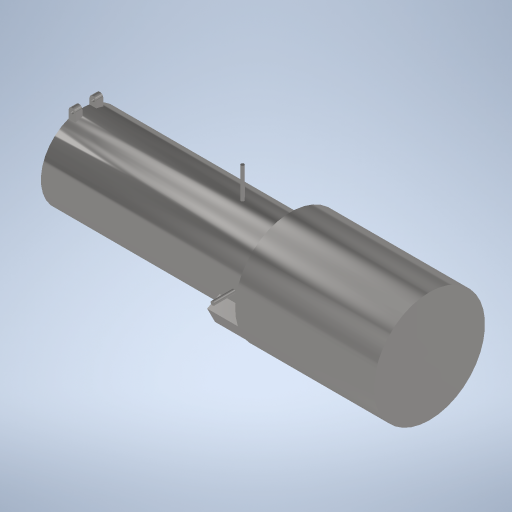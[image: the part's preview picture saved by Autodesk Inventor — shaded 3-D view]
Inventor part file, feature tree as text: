
AUTODESK INVENTOR PART (.ipt)
format: ipt  version: 2024 (Build 280153000, 153)  size: 384,000 bytes
history: native  units: mm
features: other x8, extrude x6, plane x4, mirror x2, fillet x1
ambient origin geometry x8: Origin, YZ Plane, XZ Plane, XY Plane, X Axis, Y Axis, Z Axis, Center Point
bodies: Solid1 (feature_tree)
feature tree (21):
  other  "main_body_outline"
  other  "main_body_revolution"
  plane  "Work Plane1"
  other  "utility_bay_outline"
  extrude  "utility_bay_extrude"  Depth=1500.0mm
  plane  "Work Plane2"
  other  "solar_panel_joint_outline"
  extrude  "solar_panel_joint_extrude"  Depth=900.0mm
  mirror  "solar_panel_joint_mirror"
  other  "aperature_hinge_sketch"
  extrude  "aperature_hinge_extrude"  Depth=240.0mm
  plane  "Work Plane5"
  other  "aperature_hinge_slot_sketch"
  extrude  "aperature_hinge_slot_extrude"  Depth=180.0mm
  fillet  "aperature_hinge_top_fillet"  [1 undecoded]
  other  "telescope_hole"
  extrude  "telescope_hole_extrude"  Depth=900.0mm
  plane  "Work Plane6"
  other  "antenna_slot_sketch"
  extrude  "antenna_slot_extrude"  Depth=75.088543mm
  mirror  "antenna_slot_mirror"
note: 1 required parameter value undecoded (feature->parameter linkage not recoverable at this tier; creation-order binding heuristic only, values carry confidence <= 0.55)
